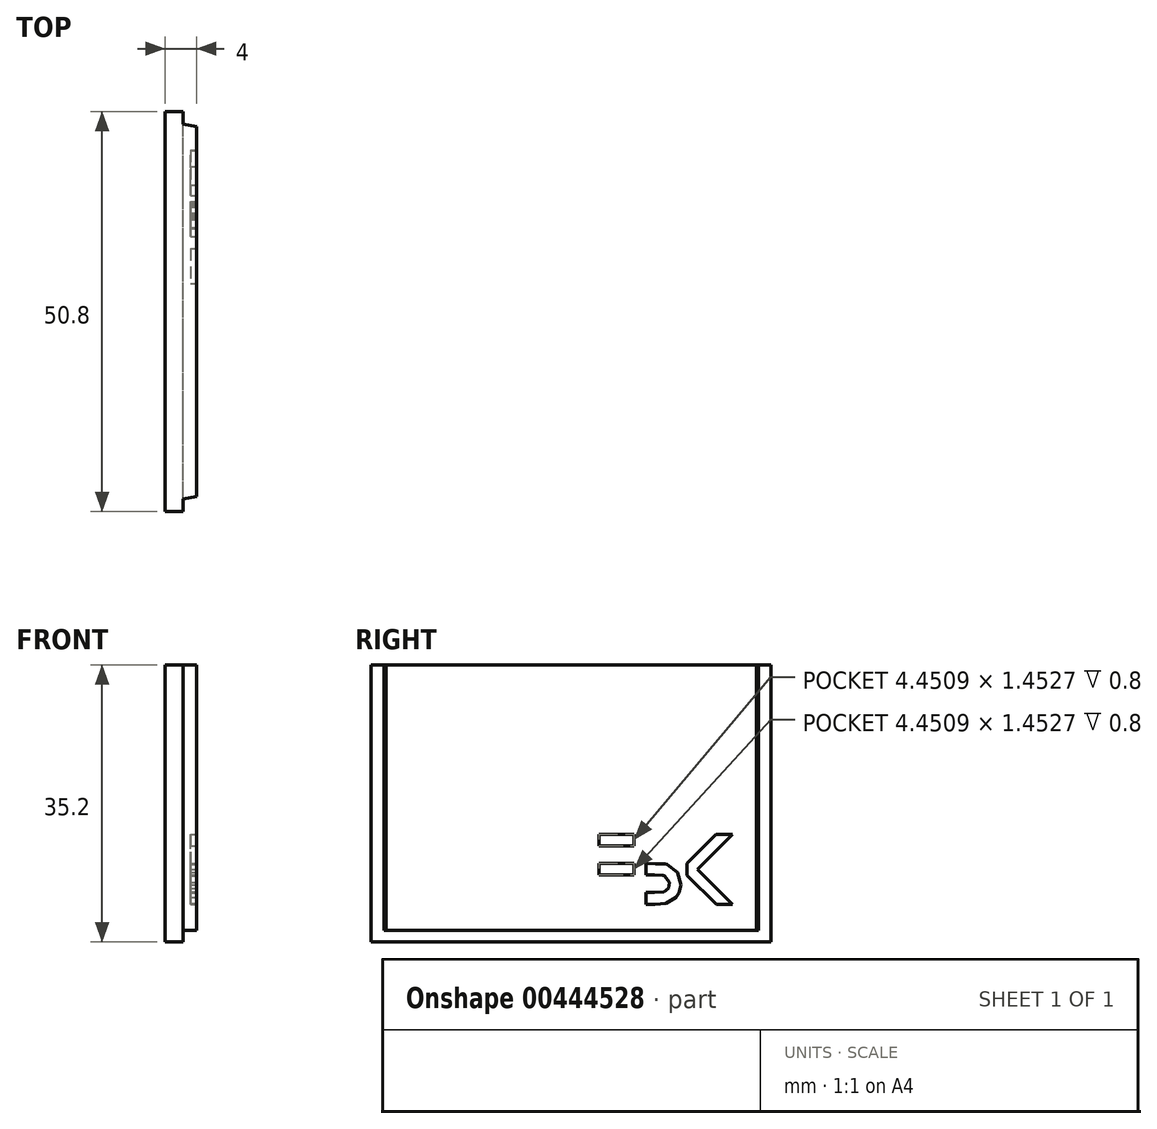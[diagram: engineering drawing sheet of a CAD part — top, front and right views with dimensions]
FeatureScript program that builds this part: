
annotation { "Feature Type Name" : "Feature", "Feature Type Description" : "" }
export const myFeature = defineFeature(function(context is Context, id is Id, definition is map)
    precondition{}
    {
        {
            var Q0;
            Q0=qCreatedBy(makeId("Top.planeOp"),FACE);
            var sketch = newSketch(context, id + "F0", { "sketchPlane" : qUnion([Q0])});
            skLineSegment(sketch, "E0.bottom", {"start": v(21.46, -52.97) * mm, "end": v(23.76, -52.97) * mm});
            skLineSegment(sketch, "E0.top", {"start": v(21.46, -2.17) * mm, "end": v(23.76, -2.17) * mm});
            skLineSegment(sketch, "E0.left", {"start": v(21.46, -52.97) * mm, "end": v(21.46, -2.17) * mm});
            skLineSegment(sketch, "E0.right", {"start": v(23.76, -52.97) * mm, "end": v(23.76, -2.17) * mm});
            skLineSegment(sketch, "E1", {"start": v(23.76, -52.97) * mm, "end": v(23.76, -51.37) * mm});
            skPoint(sketch, "E1.endSnap0", {"position": v(23.76, -27.57) * mm});
            skLineSegment(sketch, "E2", {"start": v(23.76, -51.37) * mm, "end": v(25.46, -51.37) * mm});
            skLineSegment(sketch, "E3", {"start": v(23.76, -2.17) * mm, "end": v(23.76, -3.77) * mm});
            skLineSegment(sketch, "E4", {"start": v(23.76, -3.77) * mm, "end": v(25.46, -3.77) * mm});
            skLineSegment(sketch, "E5", {"start": v(25.46, -51.37) * mm, "end": v(25.46, -3.77) * mm});
            skSolve(sketch);
        }
        {
            var Q0;
            {var subQ4=sQuery(id+"F0.wireOp",EDGE,"E0.bottom");Q0=makeQuery(id+"F0.imprint","IMPRINT",FACE,{"disambiguationData":[TD([[makeQuery(id+"F0.imprint","IMPRINT",EDGE,{"derivedFrom":subQ4}),1.0]])]});}
            var Q1;
            {var subQ0=sQuery(id+"F0.wireOp",EDGE,"E2");Q1=makeQuery(id+"F0.imprint","IMPRINT",FACE,{"disambiguationData":[TD([[makeQuery(id+"F0.imprint","IMPRINT",EDGE,{"derivedFrom":subQ0}),1.0]])]});}
            extrude(context, id + "F1", {"entities" : qUnion([Q0, Q1]), "depth" : 35.2 * mm});
        }
        {
            var Q0;
            {var subQ0=sQuery(id+"F0.wireOp",EDGE,"E2");Q0=makeQuery(id+"F0.imprint","IMPRINT",FACE,{"disambiguationData":[TD([[makeQuery(id+"F0.imprint","IMPRINT",EDGE,{"derivedFrom":subQ0}),1.0]])]});}
            extrude(context, id + "F2", {"entities" : qUnion([Q0]), "operationType" : NewBodyOperationType.REMOVE, "depth" : 1.5 * mm});
        }
        {
            var Q0;
            Q0=makeQuery(id+"F1.opExtrude","SWEPT_EDGE",EDGE,{"disambiguationData":[OSD([sQuery(id+"F0.wireOp",EDGE,"E2"),sQuery(id+"F0.wireOp",EDGE,"E5")])]});
            var Q1;
            Q1=makeQuery(id+"F2.boolean.opBoolean","COPY",EDGE,{"derivedFrom":makeQuery(id+"F2.opExtrude","CAP_EDGE",EDGE,{"disambiguationData":[OSD([sQuery(id+"F0.wireOp",EDGE,"E5")])],"isStart":false})});
            var Q2;
            Q2=makeQuery(id+"F1.opExtrude","SWEPT_EDGE",EDGE,{"disambiguationData":[OSD([sQuery(id+"F0.wireOp",EDGE,"E4"),sQuery(id+"F0.wireOp",EDGE,"E5")])]});
            chamfer(context, id + "F3", {"entities" : qUnion([Q0, Q1, Q2]), "chamferType" : ChamferType.OFFSET_ANGLE, "width" : 0.3 * mm, "oppositeDirection" : false, "angle" : 80 * degree, "tangentPropagation" : true});
        }
        {
            var Q0;
            Q0=makeQuery(id+"F1.opExtrude","SWEPT_FACE",FACE,{"disambiguationData":[OSD([sQuery(id+"F0.wireOp",EDGE,"E5")])]});
            var sketch = newSketch(context, id + "F4", { "sketchPlane" : qUnion([Q0])});
            skLineSegment(sketch, "E6", {"start": v(-18.06, 5.54) * mm, "end": v(-18.06, 6.28) * mm});
            skLineSegment(sketch, "E7", {"start": v(-18.06, 6.28) * mm, "end": v(-17, 6.28) * mm});
            skLineSegment(sketch, "E8", {"start": v(-17, 6.28) * mm, "end": v(-15.78, 6.35) * mm});
            skLineSegment(sketch, "E9", {"start": v(-15.78, 6.35) * mm, "end": v(-15.22, 6.85) * mm});
            skLineSegment(sketch, "E10", {"start": v(-15.22, 6.85) * mm, "end": v(-15.08, 7.57) * mm});
            skLineSegment(sketch, "E11", {"start": v(-15.08, 7.57) * mm, "end": v(-15.7, 8.4) * mm});
            skLineSegment(sketch, "E12", {"start": v(-15.7, 8.4) * mm, "end": v(-15.9, 8.5) * mm});
            skLineSegment(sketch, "E13", {"start": v(-15.9, 8.5) * mm, "end": v(-16.98, 8.5) * mm});
            skLineSegment(sketch, "E14", {"start": v(-16.98, 8.5) * mm, "end": v(-18.06, 8.51) * mm});
            skLineSegment(sketch, "E15", {"start": v(-18.06, 8.51) * mm, "end": v(-18.06, 9.24) * mm});
            skLineSegment(sketch, "E16", {"start": v(-18.06, 9.24) * mm, "end": v(-18.06, 9.97) * mm});
            skLineSegment(sketch, "E17", {"start": v(-18.06, 9.97) * mm, "end": v(-16.87, 9.96) * mm});
            skLineSegment(sketch, "E18", {"start": v(-16.87, 9.96) * mm, "end": v(-15.7, 9.95) * mm});
            skLineSegment(sketch, "E19", {"start": v(-15.7, 9.95) * mm, "end": v(-15.4, 9.84) * mm});
            skLineSegment(sketch, "E20", {"start": v(-15.4, 9.84) * mm, "end": v(-14.05, 8.83) * mm});
            skLineSegment(sketch, "E21", {"start": v(-14.05, 8.83) * mm, "end": v(-13.62, 7.25) * mm});
            skLineSegment(sketch, "E22", {"start": v(-13.62, 7.25) * mm, "end": v(-13.89, 6.23) * mm});
            skLineSegment(sketch, "E23", {"start": v(-13.89, 6.23) * mm, "end": v(-14.3, 5.65) * mm});
            skLineSegment(sketch, "E24", {"start": v(-14.3, 5.65) * mm, "end": v(-15.54, 4.89) * mm});
            skLineSegment(sketch, "E25", {"start": v(-15.54, 4.89) * mm, "end": v(-16.92, 4.8) * mm});
            skLineSegment(sketch, "E26", {"start": v(-16.92, 4.8) * mm, "end": v(-18.06, 4.8) * mm});
            skLineSegment(sketch, "E27", {"start": v(-18.06, 4.8) * mm, "end": v(-18.06, 5.54) * mm});
            skLineSegment(sketch, "E28", {"start": v(-2.51, -3.7) * mm, "end": v(-2.51, -3.7) * mm});
            skLineSegment(sketch, "E29", {"start": v(-11, 6.64) * mm, "end": v(-12.86, 8.48) * mm});
            skLineSegment(sketch, "E30", {"start": v(-12.86, 8.48) * mm, "end": v(-12.86, 9.23) * mm});
            skLineSegment(sketch, "E31", {"start": v(-12.86, 9.23) * mm, "end": v(-12.86, 9.98) * mm});
            skLineSegment(sketch, "E32", {"start": v(-12.86, 9.98) * mm, "end": v(-11.02, 11.82) * mm});
            skLineSegment(sketch, "E33", {"start": v(-11.02, 11.82) * mm, "end": v(-9.17, 13.67) * mm});
            skLineSegment(sketch, "E34", {"start": v(-9.17, 13.67) * mm, "end": v(-8.14, 13.67) * mm});
            skLineSegment(sketch, "E35", {"start": v(-8.14, 13.67) * mm, "end": v(-7.1, 13.67) * mm});
            skLineSegment(sketch, "E36", {"start": v(-7.1, 13.67) * mm, "end": v(-9.3, 11.46) * mm});
            skLineSegment(sketch, "E37", {"start": v(-9.3, 11.46) * mm, "end": v(-11.52, 9.25) * mm});
            skLineSegment(sketch, "E38", {"start": v(-11.52, 9.25) * mm, "end": v(-9.3, 7.03) * mm});
            skLineSegment(sketch, "E39", {"start": v(-9.3, 7.03) * mm, "end": v(-7.07, 4.8) * mm});
            skLineSegment(sketch, "E40", {"start": v(-7.07, 4.8) * mm, "end": v(-8.1, 4.8) * mm});
            skLineSegment(sketch, "E41", {"start": v(-8.1, 4.8) * mm, "end": v(-9.14, 4.8) * mm});
            skLineSegment(sketch, "E42", {"start": v(-9.14, 4.8) * mm, "end": v(-11, 6.64) * mm});
            skLineSegment(sketch, "E43", {"start": v(-24.02, 9.24) * mm, "end": v(-24.02, 9.96) * mm});
            skLineSegment(sketch, "E44", {"start": v(-24.02, 9.96) * mm, "end": v(-21.8, 9.96) * mm});
            skLineSegment(sketch, "E45", {"start": v(-21.8, 9.96) * mm, "end": v(-19.57, 9.96) * mm});
            skLineSegment(sketch, "E46", {"start": v(-19.57, 9.96) * mm, "end": v(-19.57, 9.24) * mm});
            skLineSegment(sketch, "E47", {"start": v(-19.57, 9.24) * mm, "end": v(-19.57, 8.5) * mm});
            skLineSegment(sketch, "E48", {"start": v(-19.57, 8.5) * mm, "end": v(-21.8, 8.5) * mm});
            skLineSegment(sketch, "E49", {"start": v(-21.8, 8.5) * mm, "end": v(-24.02, 8.5) * mm});
            skLineSegment(sketch, "E50", {"start": v(-24.02, 8.5) * mm, "end": v(-24.02, 9.24) * mm});
            skLineSegment(sketch, "E51", {"start": v(-24.02, 12.94) * mm, "end": v(-24.02, 13.67) * mm});
            skLineSegment(sketch, "E52", {"start": v(-24.02, 13.67) * mm, "end": v(-21.8, 13.67) * mm});
            skLineSegment(sketch, "E53", {"start": v(-21.8, 13.67) * mm, "end": v(-19.57, 13.67) * mm});
            skLineSegment(sketch, "E54", {"start": v(-19.57, 13.67) * mm, "end": v(-19.57, 12.94) * mm});
            skLineSegment(sketch, "E55", {"start": v(-19.57, 12.94) * mm, "end": v(-19.57, 12.22) * mm});
            skLineSegment(sketch, "E56", {"start": v(-19.57, 12.22) * mm, "end": v(-21.8, 12.22) * mm});
            skLineSegment(sketch, "E57", {"start": v(-21.8, 12.22) * mm, "end": v(-24.02, 12.22) * mm});
            skLineSegment(sketch, "E58", {"start": v(-24.02, 12.22) * mm, "end": v(-24.02, 12.94) * mm});
            skSolve(sketch);
        }
        {
            var Q0;
            Q0=makeQuery(id+"F4.imprint","IMPRINT",FACE,{"disambiguationData":[TD([[makeQuery(id+"F4.imprint","IMPRINT",EDGE,{"derivedFrom":sQuery(id+"F4.wireOp",EDGE,"E51")}),-1.0]])]});
            var Q1;
            Q1=makeQuery(id+"F4.imprint","IMPRINT",FACE,{"disambiguationData":[TD([[makeQuery(id+"F4.imprint","IMPRINT",EDGE,{"derivedFrom":sQuery(id+"F4.wireOp",EDGE,"E43")}),-1.0]])]});
            var Q2;
            Q2=makeQuery(id+"F4.imprint","IMPRINT",FACE,{"disambiguationData":[TD([[makeQuery(id+"F4.imprint","IMPRINT",EDGE,{"derivedFrom":sQuery(id+"F4.wireOp",EDGE,"E6")}),-1.0]])]});
            var Q3;
            Q3=makeQuery(id+"F4.imprint","IMPRINT",FACE,{"disambiguationData":[TD([[makeQuery(id+"F4.imprint","IMPRINT",EDGE,{"derivedFrom":sQuery(id+"F4.wireOp",EDGE,"E29")}),-1.0]])]});
            extrude(context, id + "F5", {"entities" : qUnion([Q0, Q1, Q2, Q3]), "operationType" : NewBodyOperationType.REMOVE, "oppositeDirection" : true, "depth" : 0.8 * mm});
        }
    });
